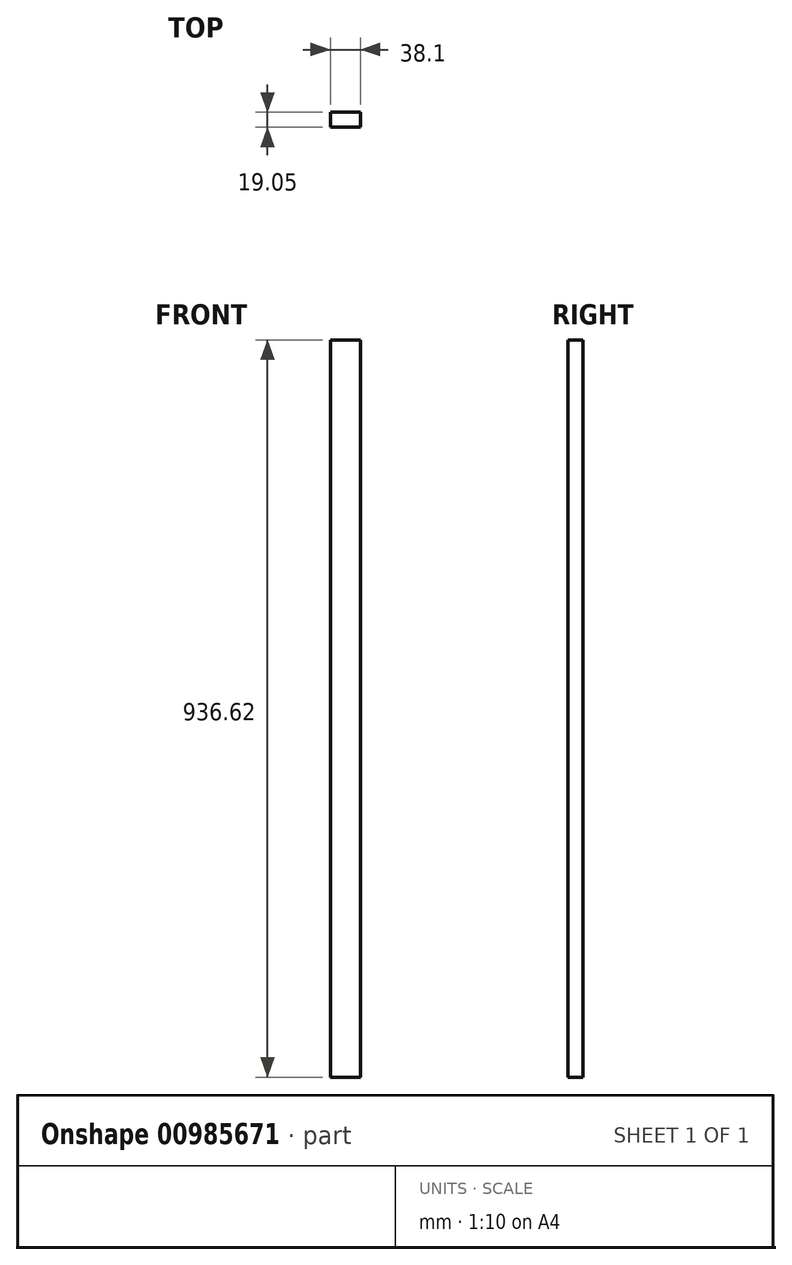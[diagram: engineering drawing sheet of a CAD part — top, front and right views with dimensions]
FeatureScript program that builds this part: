
annotation { "Feature Type Name" : "Feature", "Feature Type Description" : "" }
export const myFeature = defineFeature(function(context is Context, id is Id, definition is map)
    precondition{}
    {
        {
            var Q0;
            Q0=qCreatedBy(makeId("Front.planeOp"),FACE);
            var sketch = newSketch(context, id + "F0", { "sketchPlane" : qUnion([Q0])});
            skLineSegment(sketch, "E0.bottom", {"start": v(19.05, 468.31) * mm, "end": v(-19.05, 468.31) * mm});
            skLineSegment(sketch, "E0.top", {"start": v(19.05, -468.31) * mm, "end": v(-19.05, -468.31) * mm});
            skLineSegment(sketch, "E0.left", {"start": v(19.05, 468.31) * mm, "end": v(19.05, -468.31) * mm});
            skLineSegment(sketch, "E0.right", {"start": v(-19.05, 468.31) * mm, "end": v(-19.05, -468.31) * mm});
            skPoint(sketch, "E0.middle", {"position": v(0, 0) * mm});
            skSolve(sketch);
        }
        {
            var Q0;
            Q0=qSketchRegion(id+"F0",true);
            extrude(context, id + "F1", {"entities" : qUnion([Q0]), "depth" : 19.05 * mm, "offsetDistance" : 25.4 * mm});
        }
    });
